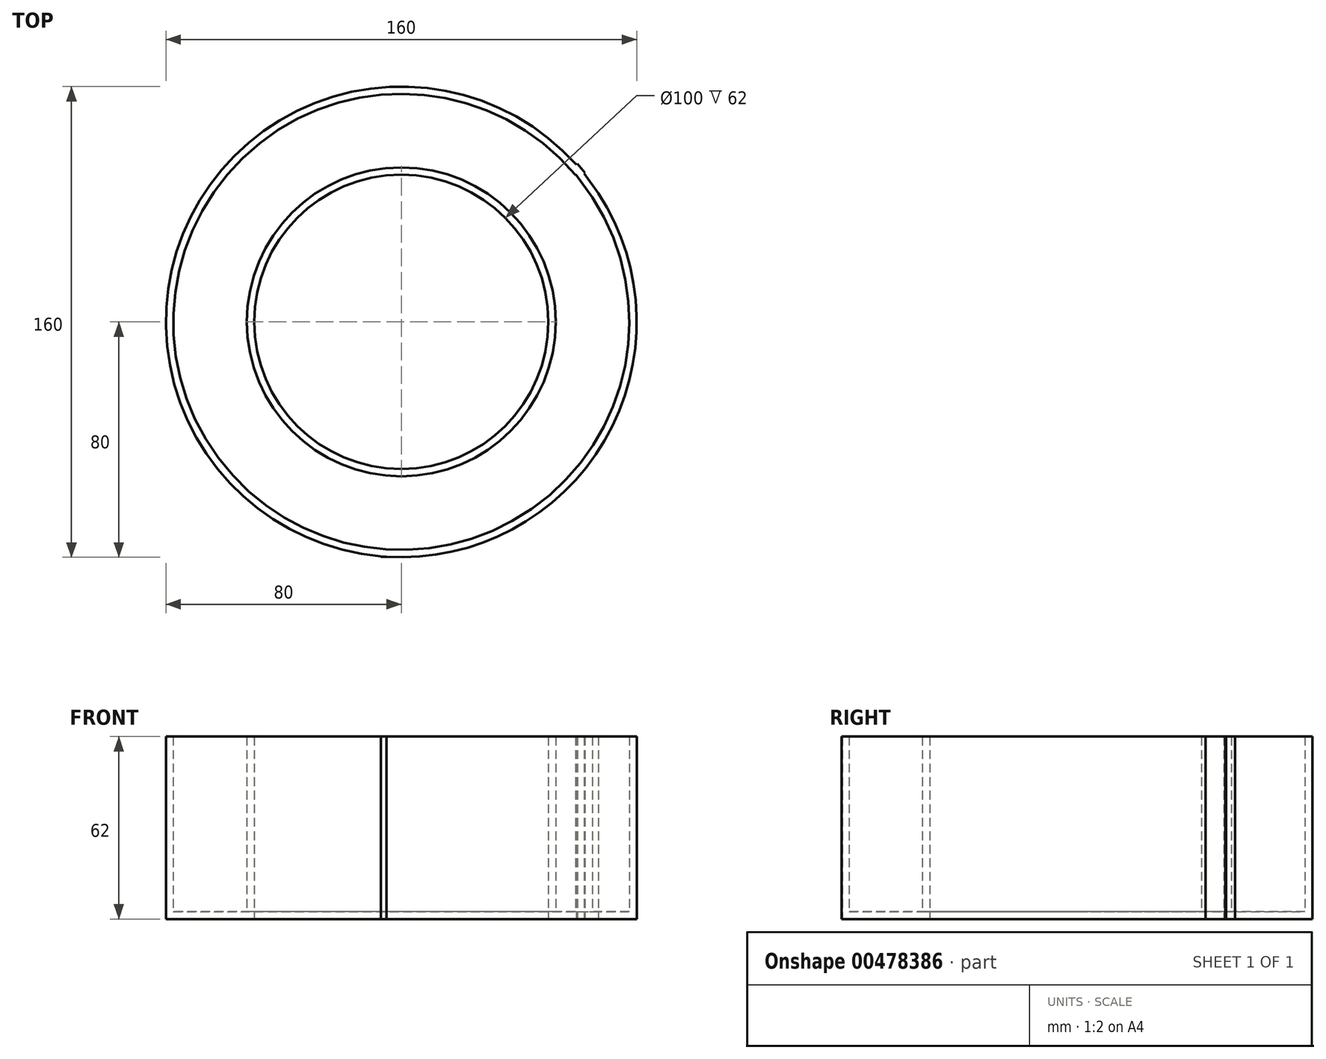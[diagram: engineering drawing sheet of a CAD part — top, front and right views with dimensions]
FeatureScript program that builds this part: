
annotation { "Feature Type Name" : "Feature", "Feature Type Description" : "" }
export const myFeature = defineFeature(function(context is Context, id is Id, definition is map)
    precondition{}
    {
        {
            var Q0;
            Q0=qCreatedBy(makeId("Top.planeOp"),FACE);
            var sketch = newSketch(context, id + "F0", { "sketchPlane" : qUnion([Q0])});
            skArc(sketch, "E0", {"start": v(62.1, 50.42) * mm, "mid": v(-64.64, -47.13) * mm, "end": v(67, 43.72) * mm});
            skLineSegment(sketch, "E1.bottom", {"start": v(-7.22, 79.67) * mm, "end": v(4.78, 79.67) * mm});
            skLineSegment(sketch, "E1.left", {"start": v(-7.22, 79.67) * mm, "end": v(-7.22, 49.77) * mm});
            skLineSegment(sketch, "E1.right", {"start": v(4.78, 79.67) * mm, "end": v(4.78, 49.77) * mm});
            skLineSegment(sketch, "E2.bottom", {"start": v(4.78, -49.51) * mm, "end": v(5.03, -49.51) * mm});
            skLineSegment(sketch, "E2.top", {"start": v(-6.97, -79.84) * mm, "end": v(5.03, -79.84) * mm});
            skLineSegment(sketch, "E2.left", {"start": v(-6.97, -49.51) * mm, "end": v(-6.97, -79.84) * mm});
            skLineSegment(sketch, "E2.right", {"start": v(5.03, -49.51) * mm, "end": v(5.03, -79.84) * mm});
            skLineSegment(sketch, "E3", {"start": v(-80, 0) * mm, "end": v(-50, 0) * mm});
            skLineSegment(sketch, "E4", {"start": v(50, 0) * mm, "end": v(80, 0) * mm});
            skLineSegment(sketch, "E5", {"start": v(-71.13, -36.62) * mm, "end": v(-43.97, -23.8) * mm});
            skLineSegment(sketch, "E6", {"start": v(44.1, 23.57) * mm, "end": v(73.74, 31.03) * mm});
            skLineSegment(sketch, "E7", {"start": v(-61.4, 51.28) * mm, "end": v(-37.56, 33) * mm});
            skCircle(sketch, "E8", {"center": v(0, 0) * mm, "radius": 40 * mm});
            skArc(sketch, "E9", {"start": v(5.03, -49.75) * mm, "mid": v(50, 0.13) * mm, "end": v(4.78, 49.77) * mm});
            skArc(sketch, "E10.trimOffspring", {"start": v(-37.56, 33) * mm, "mid": v(-46.88, -17.38) * mm, "end": v(-6.97, -49.51) * mm});
            skArc(sketch, "E11", {"start": v(39.2, 31.03) * mm, "mid": v(-41.82, -27.4) * mm, "end": v(44.1, 23.57) * mm});
            skCircle(sketch, "E12", {"center": v(0, 0) * mm, "radius": 12.5 * mm});
            skLineSegment(sketch, "E13.bottom", {"start": v(36.4, 34.07) * mm, "end": v(59.8, 53.71) * mm});
            skLineSegment(sketch, "E13.top", {"start": v(38.97, 31) * mm, "end": v(39.12, 31.14) * mm});
            skLineSegment(sketch, "E13.left", {"start": v(36.4, 34.07) * mm, "end": v(38.97, 31) * mm});
            skLineSegment(sketch, "E13.right", {"start": v(59.8, 53.71) * mm, "end": v(62.37, 50.65) * mm});
            skLineSegment(sketch, "E14.trimOffspring", {"start": v(62.1, 50.42) * mm, "end": v(62.37, 50.65) * mm});
            skPoint(sketch, "E15.end.orphan", {"position": v(39.2, 31.03) * mm});
            skPoint(sketch, "E15.start.orphan", {"position": v(67, 43.72) * mm});
            skLineSegment(sketch, "E16", {"start": v(59.8, 53.71) * mm, "end": v(67, 43.72) * mm});
            skSolve(sketch);
        }
        {
            var Q0;
            Q0 = qSketchRegion(id + "F0", true);
            extrude(context, id + "F1", {"entities" : qUnion([Q0]), "depth" : 62 * mm, "offsetDistance" : 25 * mm});
        }
        {
            var Q0;
            Q0=makeQuery(id+"F1.opExtrude","CAP_FACE",FACE,{"disambiguationData":[OSD([sQuery(id+"F0.wireOp",EDGE,"E0"),sQuery(id+"F0.wireOp",EDGE,"E2.top"),sQuery(id+"F0.wireOp",EDGE,"E2.left"),sQuery(id+"F0.wireOp",EDGE,"E9"),sQuery(id+"F0.wireOp",EDGE,"E11"),sQuery(id+"F0.wireOp",EDGE,"E13.bottom"),sQuery(id+"F0.wireOp",EDGE,"E13.right"),sQuery(id+"F0.wireOp",EDGE,"E14.trimOffspring"),sQuery(id+"F0.wireOp",EDGE,"E16")])],"isStart":false});
            shell(context, id + "F2", {"entities" : qUnion([Q0]), "thickness" : 2.5 * mm});
        }
    });
